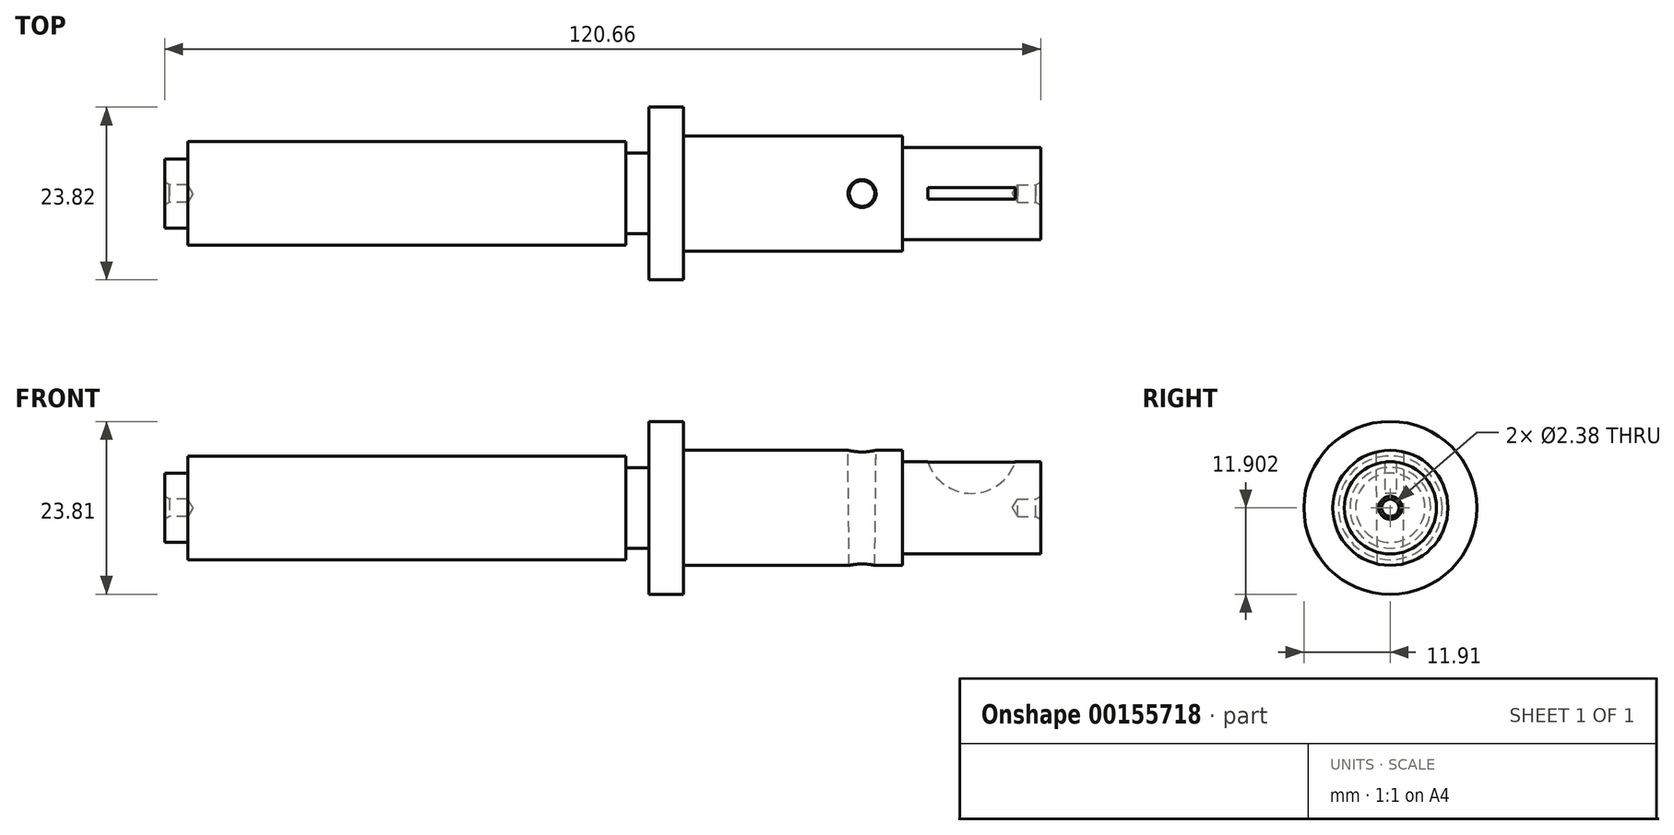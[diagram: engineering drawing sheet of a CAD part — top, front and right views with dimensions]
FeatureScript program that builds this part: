
annotation { "Feature Type Name" : "Feature", "Feature Type Description" : "" }
export const myFeature = defineFeature(function(context is Context, id is Id, definition is map)
    precondition{}
    {
        {
            var Q0;
            Q0=qCreatedBy(makeId("Front.planeOp"),FACE);
            var sketch = newSketch(context, id + "F5", { "sketchPlane" : qUnion([Q0])});
            skLineSegment(sketch, "E0", {"start": v(-60.33, -7.94) * mm, "end": v(60.33, -7.94) * mm});
            skLineSegment(sketch, "E1", {"start": v(60.33, -7.94) * mm, "end": v(60.33, -1.59) * mm});
            skLineSegment(sketch, "E2", {"start": v(60.33, -1.59) * mm, "end": v(41.28, -1.59) * mm});
            skLineSegment(sketch, "E3", {"start": v(41.28, -1.59) * mm, "end": v(41.28, 0) * mm});
            skLineSegment(sketch, "E4", {"start": v(41.28, 0) * mm, "end": v(11.11, 0) * mm});
            skLineSegment(sketch, "E5", {"start": v(11.11, 0) * mm, "end": v(11.11, 3.97) * mm});
            skLineSegment(sketch, "E6", {"start": v(11.11, 3.97) * mm, "end": v(6.35, 3.97) * mm});
            skLineSegment(sketch, "E7", {"start": v(6.35, 3.97) * mm, "end": v(6.35, -2.38) * mm});
            skLineSegment(sketch, "E8", {"start": v(6.35, -2.38) * mm, "end": v(3.18, -2.38) * mm});
            skLineSegment(sketch, "E9", {"start": v(3.18, -2.38) * mm, "end": v(3.18, -0.8) * mm});
            skLineSegment(sketch, "E10", {"start": v(3.18, -0.8) * mm, "end": v(-57.15, -0.8) * mm});
            skLineSegment(sketch, "E11", {"start": v(-57.15, -0.8) * mm, "end": v(-57.15, -3.17) * mm});
            skLineSegment(sketch, "E12", {"start": v(-57.15, -3.17) * mm, "end": v(-60.33, -3.17) * mm});
            skLineSegment(sketch, "E13", {"start": v(-60.33, -3.17) * mm, "end": v(-60.32, -7.94) * mm});
            skSolve(sketch);
        }
        {
            var Q0;
            Q0 = qSketchRegion(id + "F5", true);
            var Q1;
            Q1=sQuery(id+"F5.wireOp",EDGE,"E0");
            revolve(context, id + "F0", {"entities" : qUnion([Q0]), "axis" : qUnion([Q1]), "revolveType" : RevolveType.FULL});
        }
        {
            var Q0;
            Q0=qCreatedBy(makeId("Front.planeOp"),FACE);
            var sketch = newSketch(context, id + "F1", { "sketchPlane" : qUnion([Q0])});
            skCircle(sketch, "E14", {"center": v(50.8, 0.4) * mm, "radius": 6.35 * mm});
            skSolve(sketch);
        }
        {
            var Q0;
            Q0 = qSketchRegion(id + "F1", true);
            extrude(context, id + "F6", {"entities" : qUnion([Q0]), "operationType" : NewBodyOperationType.REMOVE, "endBound" : BoundingType.SYMMETRIC, "oppositeDirection" : true, "depth" : 1.59 * mm});
        }
        {
            var Q0;
            Q0=qCreatedBy(makeId("Front.planeOp"),FACE);
            var sketch = newSketch(context, id + "F2", { "sketchPlane" : qUnion([Q0])});
            skLineSegment(sketch, "E15", {"start": v(35.72, 28.27) * mm, "end": v(35.72, -28.27) * mm, "construction": true});
            skLineSegment(sketch, "E16", {"start": v(37.7, 4.34) * mm, "end": v(37.43, -20.32) * mm});
            skLineSegment(sketch, "E17", {"start": v(35.72, 4.76) * mm, "end": v(35.72, -20.64) * mm});
            skArc(sketch, "E18", {"start": v(37.7, 4.34) * mm, "mid": v(36.73, 4.66) * mm, "end": v(35.72, 4.76) * mm});
            skArc(sketch, "E19", {"start": v(35.72, -20.64) * mm, "mid": v(36.6, -20.56) * mm, "end": v(37.43, -20.32) * mm});
            skSolve(sketch);
        }
        {
            var Q0;
            Q0 = qSketchRegion(id + "F2", true);
            var Q1;
            Q1=sQuery(id+"F2.wireOp",EDGE,"E15");
            revolve(context, id + "F7", {"operationType" : NewBodyOperationType.REMOVE, "entities" : qUnion([Q0]), "axis" : qUnion([Q1]), "revolveType" : RevolveType.FULL, "oppositeDirection" : true});
        }
        {
            var Q0;
            Q0=makeQuery(id+"F0.opRevolve","SWEPT_FACE",FACE,{"disambiguationData":[OSD([sQuery(id+"F5.wireOp",EDGE,"E1")])]});
            var sketch = newSketch(context, id + "F3", { "sketchPlane" : qUnion([Q0])});
            skPoint(sketch, "E20", {"position": v(0, -7.94) * mm});
            skSolve(sketch);
        }
        {
            var Q0;
            Q0=makeQuery(id+"F0.opRevolve","SWEPT_FACE",FACE,{"disambiguationData":[OSD([sQuery(id+"F5.wireOp",EDGE,"E13")])]});
            var sketch = newSketch(context, id + "F8", { "sketchPlane" : qUnion([Q0])});
            skPoint(sketch, "E21.0", {"position": v(0, -7.94) * mm});
            skSolve(sketch);
        }
        {
            var Q0;
            Q0=sQuery(id+"F3.wireOp",VERTEX,"E20");
            var Q1;
            Q1=sQuery(id+"F8.wireOp",VERTEX,"E21.0");
            var Q2;
            Q2=makeQuery(id+"F0.opRevolve","SWEPT_BODY",BODY,{"disambiguationData":[OSD([sQuery(id+"F5.wireOp",EDGE,"E0"),sQuery(id+"F5.wireOp",EDGE,"E1"),sQuery(id+"F5.wireOp",EDGE,"E2"),sQuery(id+"F5.wireOp",EDGE,"E3"),sQuery(id+"F5.wireOp",EDGE,"E4"),sQuery(id+"F5.wireOp",EDGE,"E5"),sQuery(id+"F5.wireOp",EDGE,"E6"),sQuery(id+"F5.wireOp",EDGE,"E7"),sQuery(id+"F5.wireOp",EDGE,"E8"),sQuery(id+"F5.wireOp",EDGE,"E9"),sQuery(id+"F5.wireOp",EDGE,"E10"),sQuery(id+"F5.wireOp",EDGE,"E11"),sQuery(id+"F5.wireOp",EDGE,"E12"),sQuery(id+"F5.wireOp",EDGE,"E13")])]});
            hole(context, id + "F4", {"style" : HoleStyle.C_SINK, "endStyle" : HoleEndStyle.BLIND, "holeDiameter" : 2.38 * mm, "cSinkDiameter" : 3.14 * mm, "cSinkAngle" : 60 * degree, "holeDepth" : 3.17 * mm, "locations" : qUnion([Q0, Q1]), "scope" : qUnion([Q2])});
        }
    });
